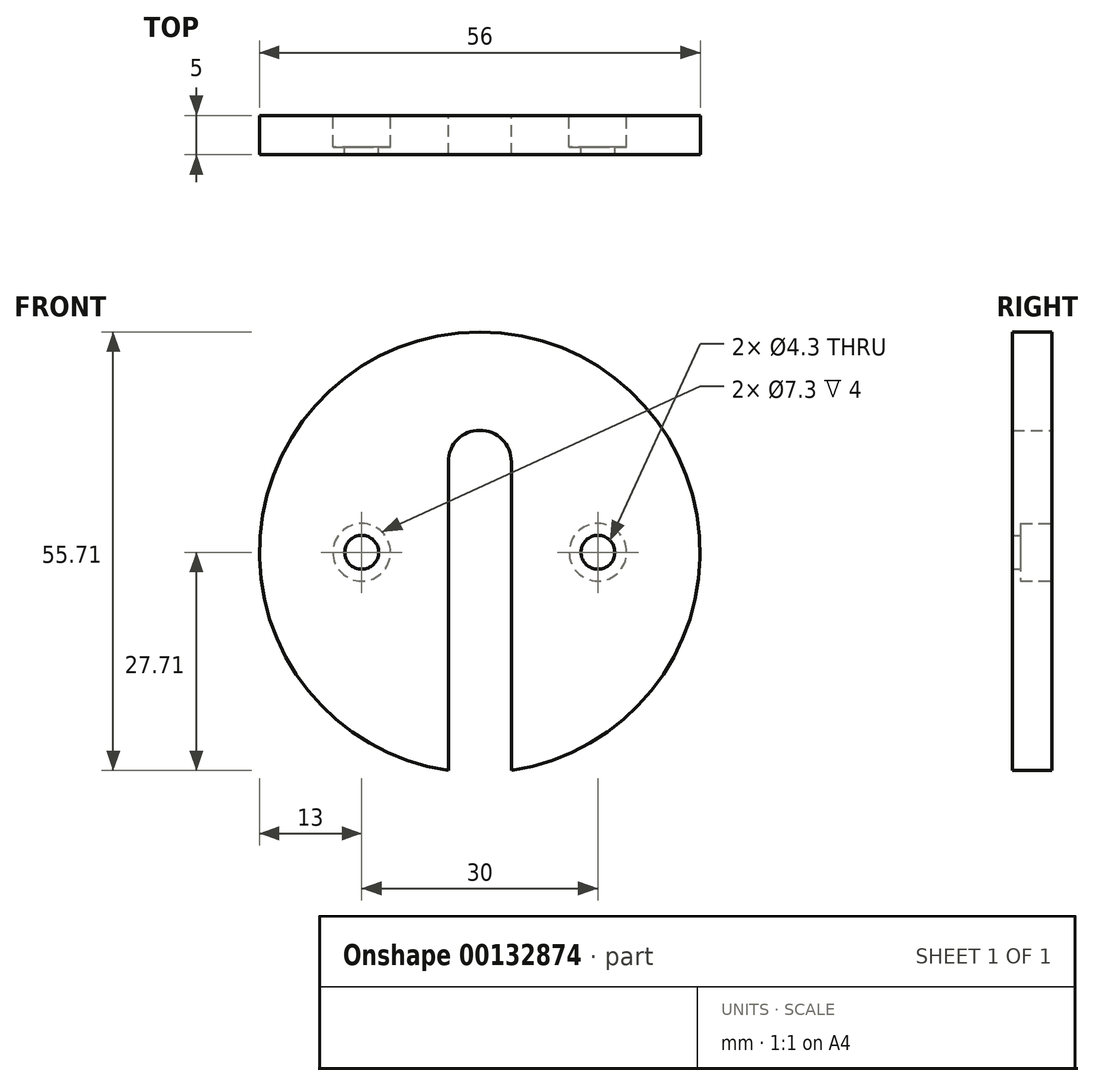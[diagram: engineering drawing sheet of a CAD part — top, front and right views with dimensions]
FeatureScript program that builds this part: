
annotation { "Feature Type Name" : "Feature", "Feature Type Description" : "" }
export const myFeature = defineFeature(function(context is Context, id is Id, definition is map)
    precondition{}
    {
        {
            var Q0;
            Q0=qCreatedBy(makeId("Front.planeOp"),FACE);
            var sketch = newSketch(context, id + "F0", { "sketchPlane" : qUnion([Q0])});
            skCircle(sketch, "E0", {"center": v(0, 0) * mm, "radius": 28 * mm});
            skSolve(sketch);
        }
        {
            var Q0;
            Q0 = qSketchRegion(id + "F0", true);
            extrude(context, id + "F1", {"entities" : qUnion([Q0]), "depth" : 5 * mm});
        }
        {
            var Q0;
            Q0=makeQuery(id+"F1.opExtrude","CAP_FACE",FACE,{"disambiguationData":[OSD([sQuery(id+"F0.wireOp",EDGE,"E0")])],"isStart":true});
            var sketch = newSketch(context, id + "F2", { "sketchPlane" : qUnion([Q0])});
            skLineSegment(sketch, "E1", {"start": v(-4, 11.5) * mm, "end": v(-4, -27.71) * mm});
            skLineSegment(sketch, "E2", {"start": v(4, 11.5) * mm, "end": v(4, -27.71) * mm});
            skArc(sketch, "E3", {"start": v(4, 11.5) * mm, "mid": v(0, 15.5) * mm, "end": v(-4, 11.5) * mm});
            skArc(sketch, "E4", {"start": v(-4, -27.71) * mm, "mid": v(0, -28) * mm, "end": v(4, -27.71) * mm});
            skSolve(sketch);
        }
        {
            var Q0;
            Q0 = qSketchRegion(id + "F2", true);
            extrude(context, id + "F3", {"entities" : qUnion([Q0]), "operationType" : NewBodyOperationType.REMOVE, "oppositeDirection" : true, "depth" : 35 * mm});
        }
        {
            var Q0;
            Q0=makeQuery(id+"F1.opExtrude","CAP_FACE",FACE,{"disambiguationData":[OSD([sQuery(id+"F0.wireOp",EDGE,"E0")])],"isStart":true});
            var sketch = newSketch(context, id + "F4", { "sketchPlane" : qUnion([Q0])});
            skCircle(sketch, "E5", {"center": v(-15, 0) * mm, "radius": 2.15 * mm});
            skCircle(sketch, "E6", {"center": v(15, 0) * mm, "radius": 2.15 * mm});
            skPoint(sketch, "E7.trimOffspring.center.orphan", {"position": v(0, 0) * mm});
            skSolve(sketch);
        }
        {
            var Q0;
            Q0 = qSketchRegion(id + "F4", true);
            extrude(context, id + "F5", {"entities" : qUnion([Q0]), "operationType" : NewBodyOperationType.REMOVE, "oppositeDirection" : true, "depth" : 25 * mm});
        }
        {
            var Q0;
            Q0=makeQuery(id+"F1.opExtrude","CAP_FACE",FACE,{"disambiguationData":[OSD([sQuery(id+"F0.wireOp",EDGE,"E0")])],"isStart":true});
            var sketch = newSketch(context, id + "F6", { "sketchPlane" : qUnion([Q0])});
            skCircle(sketch, "E8", {"center": v(-15, 0) * mm, "radius": 3.65 * mm});
            skCircle(sketch, "E9", {"center": v(15, 0) * mm, "radius": 3.65 * mm});
            skSolve(sketch);
        }
        {
            var Q0;
            Q0 = qSketchRegion(id + "F6", true);
            extrude(context, id + "F7", {"entities" : qUnion([Q0]), "operationType" : NewBodyOperationType.REMOVE, "oppositeDirection" : true, "depth" : 4 * mm});
        }
    });
